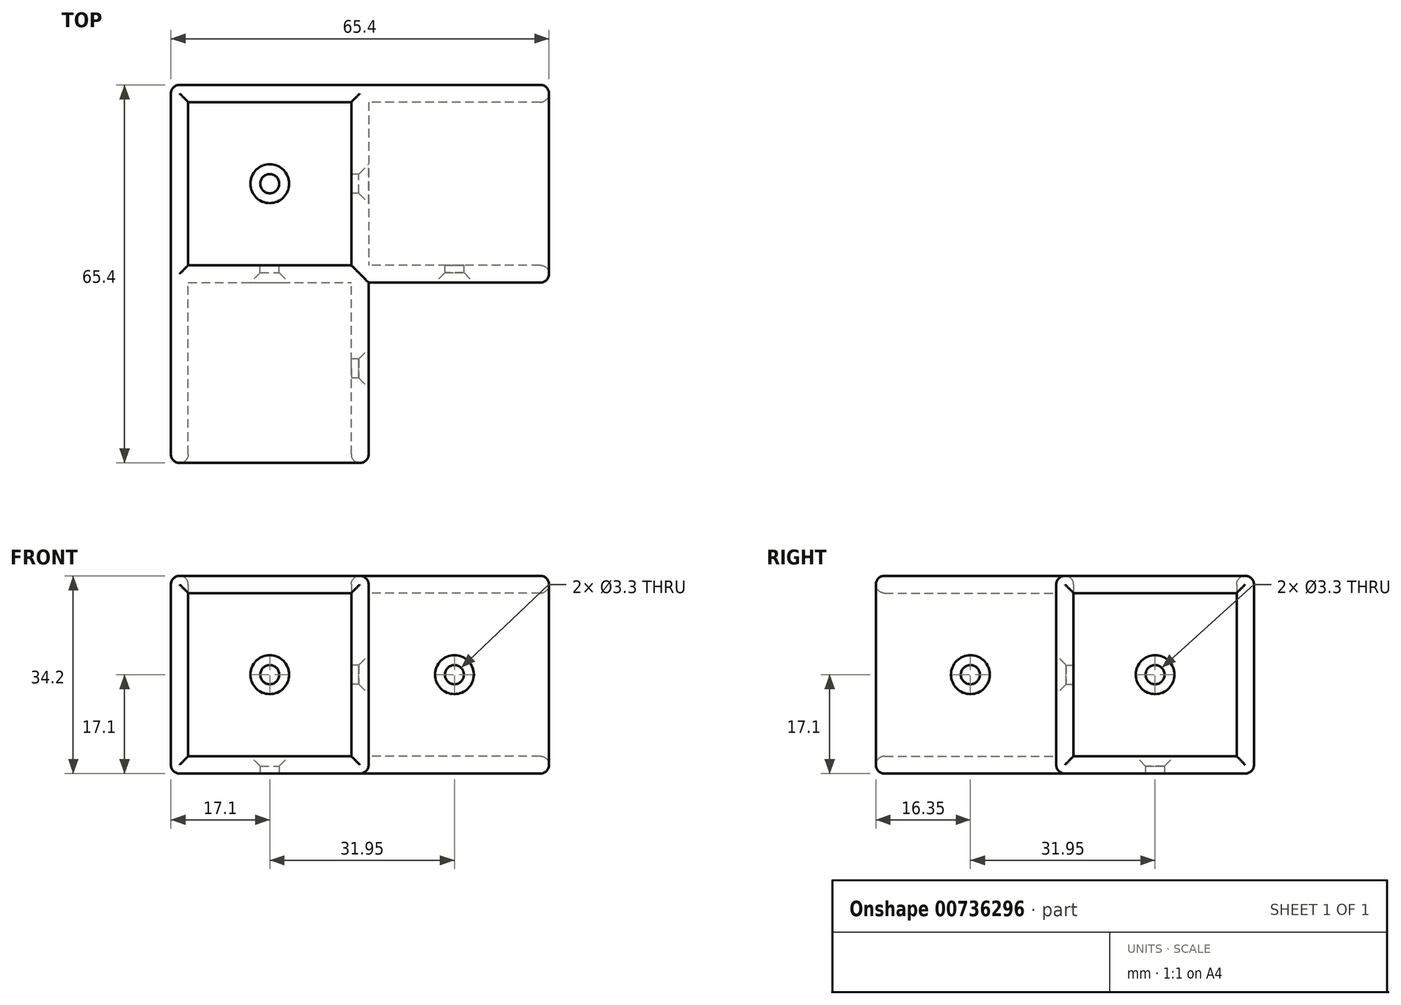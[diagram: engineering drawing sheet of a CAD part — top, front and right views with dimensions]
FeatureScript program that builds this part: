
annotation { "Feature Type Name" : "Feature", "Feature Type Description" : "" }
export const myFeature = defineFeature(function(context is Context, id is Id, definition is map)
    precondition{}
    {
        {
            var Q0;
            Q0=qCreatedBy(makeId("Top.planeOp"),FACE);
            var sketch = newSketch(context, id + "F0", { "sketchPlane" : qUnion([Q0])});
            skLineSegment(sketch, "E0.bottom", {"start": v(0, 0) * mm, "end": v(-28.2, 0) * mm});
            skLineSegment(sketch, "E0.top", {"start": v(0, 28.2) * mm, "end": v(-28.2, 28.2) * mm});
            skLineSegment(sketch, "E0.left", {"start": v(0, 0) * mm, "end": v(0, 28.2) * mm});
            skLineSegment(sketch, "E0.right", {"start": v(-28.2, 0) * mm, "end": v(-28.2, 28.2) * mm});
            skLineSegment(sketch, "E1.0", {"start": v(3, 31.2) * mm, "end": v(-31.2, 31.2) * mm});
            skLineSegment(sketch, "E1.1", {"start": v(3, -3) * mm, "end": v(3, 31.2) * mm});
            skLineSegment(sketch, "E1.2", {"start": v(3, -3) * mm, "end": v(-31.2, -3) * mm});
            skLineSegment(sketch, "E1.3", {"start": v(-31.2, -3) * mm, "end": v(-31.2, 31.2) * mm});
            skPoint(sketch, "E2", {"position": v(-14.1, 14.1) * mm});
            skSolve(sketch);
        }
        {
            var Q0;
            Q0=makeQuery(id+"F0.imprint","IMPRINT",FACE,{"disambiguationData":[TD([[makeQuery(id+"F0.imprint","IMPRINT",EDGE,{"derivedFrom":sQuery(id+"F0.wireOp",EDGE,"E0.bottom")}),1.0]])]});
            var Q1;
            Q1=makeQuery(id+"F0.imprint","IMPRINT",FACE,{"disambiguationData":[TD([[makeQuery(id+"F0.imprint","IMPRINT",EDGE,{"derivedFrom":sQuery(id+"F0.wireOp",EDGE,"E0.bottom")}),-1.0]])]});
            extrude(context, id + "F1", {"entities" : qUnion([Q0, Q1]), "oppositeDirection" : true, "depth" : 3 * mm, "offsetDistance" : 25 * mm});
        }
        {
            var Q0;
            Q0=makeQuery(id+"F0.imprint","IMPRINT",FACE,{"disambiguationData":[TD([[makeQuery(id+"F0.imprint","IMPRINT",EDGE,{"derivedFrom":sQuery(id+"F0.wireOp",EDGE,"E0.bottom")}),1.0]])]});
            extrude(context, id + "F2", {"entities" : qUnion([Q0]), "operationType" : NewBodyOperationType.ADD, "depth" : 31.2 * mm, "offsetDistance" : 25 * mm});
        }
        {
            var Q0;
            {var subQ0=sQuery(id+"F0.wireOp",EDGE,"E1.2");Q0=makeQuery(id+"F2.boolean.opBoolean","MERGE",FACE,{"derivedFrom":[makeQuery(id+"F1.opExtrude","SWEPT_FACE",FACE,{"disambiguationData":[OSD([subQ0])]}),makeQuery(id+"F2.opExtrude","SWEPT_FACE",FACE,{"disambiguationData":[OSD([subQ0])]})]});}
            var sketch = newSketch(context, id + "F3", { "sketchPlane" : qUnion([Q0])});
            skLineSegment(sketch, "E3.bottom", {"start": v(-31.2, 31.2) * mm, "end": v(3, 31.2) * mm});
            skLineSegment(sketch, "E3.top", {"start": v(-31.2, -3) * mm, "end": v(3, -3) * mm});
            skLineSegment(sketch, "E3.left", {"start": v(-31.2, 31.2) * mm, "end": v(-31.2, -3) * mm});
            skLineSegment(sketch, "E3.right", {"start": v(3, 31.2) * mm, "end": v(3, -3) * mm});
            skLineSegment(sketch, "E4.0", {"start": v(-28.2, 28.2) * mm, "end": v(0, 28.2) * mm});
            skLineSegment(sketch, "E4.1", {"start": v(-28.2, 28.2) * mm, "end": v(-28.2, 0) * mm});
            skLineSegment(sketch, "E4.2", {"start": v(-28.2, 0) * mm, "end": v(0, 0) * mm});
            skLineSegment(sketch, "E4.3", {"start": v(0, 28.2) * mm, "end": v(0, 0) * mm});
            skPoint(sketch, "E5", {"position": v(-14.1, 14.1) * mm});
            skSolve(sketch);
        }
        {
            var Q0;
            Q0=makeQuery(id+"F3.imprint","IMPRINT",FACE,{"disambiguationData":[TD([[makeQuery(id+"F3.imprint","IMPRINT",EDGE,{"derivedFrom":sQuery(id+"F3.wireOp",EDGE,"E3.bottom")}),1.0]])]});
            extrude(context, id + "F4", {"entities" : qUnion([Q0]), "operationType" : NewBodyOperationType.ADD, "depth" : 31.2 * mm, "offsetDistance" : 25 * mm});
        }
        {
            var Q0;
            {var subQ0=sQuery(id+"F0.wireOp",EDGE,"E1.1");Q0=makeQuery(id+"F4.boolean.opBoolean","MERGE",FACE,{"derivedFrom":[makeQuery(id+"F2.boolean.opBoolean","MERGE",FACE,{"derivedFrom":[makeQuery(id+"F1.opExtrude","SWEPT_FACE",FACE,{"disambiguationData":[OSD([subQ0])]}),makeQuery(id+"F2.opExtrude","SWEPT_FACE",FACE,{"disambiguationData":[OSD([subQ0])]})]}),makeQuery(id+"F4.opExtrude","SWEPT_FACE",FACE,{"disambiguationData":[OSD([sQuery(id+"F3.wireOp",EDGE,"E3.right")])]})]});}
            var sketch = newSketch(context, id + "F5", { "sketchPlane" : qUnion([Q0])});
            skLineSegment(sketch, "E6.bottom", {"start": v(31.2, 31.2) * mm, "end": v(-3, 31.2) * mm});
            skLineSegment(sketch, "E6.top", {"start": v(31.2, -3) * mm, "end": v(-3, -3) * mm});
            skLineSegment(sketch, "E6.left", {"start": v(31.2, 31.2) * mm, "end": v(31.2, -3) * mm});
            skLineSegment(sketch, "E6.right", {"start": v(-3, 31.2) * mm, "end": v(-3, -3) * mm});
            skLineSegment(sketch, "E7.0", {"start": v(28.2, 28.2) * mm, "end": v(0, 28.2) * mm});
            skLineSegment(sketch, "E7.1", {"start": v(28.2, 28.2) * mm, "end": v(28.2, 0) * mm});
            skLineSegment(sketch, "E7.2", {"start": v(28.2, 0) * mm, "end": v(0, 0) * mm});
            skLineSegment(sketch, "E7.3", {"start": v(0, 28.2) * mm, "end": v(0, 0) * mm});
            skPoint(sketch, "E8", {"position": v(14.1, 14.1) * mm});
            skSolve(sketch);
        }
        {
            var Q0;
            Q0 = qSketchRegion(id + "F5", true);
            extrude(context, id + "F6", {"entities" : qUnion([Q0]), "operationType" : NewBodyOperationType.ADD, "depth" : 31.2 * mm, "offsetDistance" : 25 * mm});
        }
        {
            var Q0;
            Q0=sQuery(id+"F0.wireOp",VERTEX,"E2");
            var Q1;
            Q1=sQuery(id+"F5.wireOp",VERTEX,"E8");
            var Q2;
            Q2=sQuery(id+"F3.wireOp",VERTEX,"E5");
            var Q3;
            Q3=makeQuery(id+"F1.opExtrude","SWEPT_BODY",BODY,{"disambiguationData":[OSD([sQuery(id+"F0.wireOp",EDGE,"E1.0"),sQuery(id+"F0.wireOp",EDGE,"E1.1"),sQuery(id+"F0.wireOp",EDGE,"E1.2"),sQuery(id+"F0.wireOp",EDGE,"E1.3")])]});
            hole(context, id + "F7", {"style" : HoleStyle.C_SINK, "endStyle" : HoleEndStyle.BLIND, "standardTappedOrClearance" : lookupTablePath({ "standard" : "ISO", "fit" : "Normal", "size" : "M3", "type" : "Clearance" }), "standardBlindInLast" : lookupTablePath({ "fit" : "Standard", "standard" : "ISO", "size" : "M3", "type" : "Clearance" }), "holeDiameter" : 3.3 * mm, "cSinkDiameter" : 6.72 * mm, "cSinkAngle" : 90 * degree, "majorDiameter" : 5 * mm, "holeDepth" : 13.5 * mm, "isTappedThrough" : true, "tappedDepth" : 12 * mm, "tapClearance" : 3, "startFromSketch" : true, "locations" : qUnion([Q0, Q1, Q2]), "scope" : qUnion([Q3])});
        }
        {
            var Q0;
            Q0=makeQuery(id+"F4.boolean.opBoolean","MERGE",EDGE,{"derivedFrom":[makeQuery(id+"F2.opExtrude","CAP_EDGE",EDGE,{"disambiguationData":[OSD([sQuery(id+"F0.wireOp",EDGE,"E1.3")])],"isStart":false}),makeQuery(id+"F4.opExtrude","SWEPT_EDGE",EDGE,{"disambiguationData":[OSD([sQuery(id+"F3.wireOp",EDGE,"E3.bottom"),sQuery(id+"F3.wireOp",EDGE,"E3.left")])]})]});
            var Q1;
            Q1=makeQuery(id+"F6.boolean.opBoolean","MERGE",EDGE,{"derivedFrom":[makeQuery(id+"F2.opExtrude","CAP_EDGE",EDGE,{"disambiguationData":[OSD([sQuery(id+"F0.wireOp",EDGE,"E1.0")])],"isStart":false}),makeQuery(id+"F6.opExtrude","SWEPT_EDGE",EDGE,{"disambiguationData":[OSD([sQuery(id+"F5.wireOp",EDGE,"E6.bottom"),sQuery(id+"F5.wireOp",EDGE,"E6.left")])]})]});
            var Q2;
            Q2=makeQuery(id+"F6.opExtrude","CAP_EDGE",EDGE,{"disambiguationData":[OSD([sQuery(id+"F5.wireOp",EDGE,"E6.bottom")])],"isStart":false});
            var Q3;
            Q3=makeQuery(id+"F6.opExtrude","SWEPT_EDGE",EDGE,{"disambiguationData":[OSD([sQuery(id+"F0.wireOp",EDGE,"E1.1"),sQuery(id+"F3.wireOp",EDGE,"E3.bottom"),sQuery(id+"F3.wireOp",EDGE,"E3.right"),sQuery(id+"F5.wireOp",EDGE,"E6.bottom"),sQuery(id+"F5.wireOp",EDGE,"E6.right")])]});
            var Q4;
            Q4=makeQuery(id+"F4.boolean.opBoolean","MERGE",EDGE,{"derivedFrom":[makeQuery(id+"F2.opExtrude","CAP_EDGE",EDGE,{"disambiguationData":[OSD([sQuery(id+"F0.wireOp",EDGE,"E1.1")])],"isStart":false}),makeQuery(id+"F4.opExtrude","SWEPT_EDGE",EDGE,{"disambiguationData":[OSD([sQuery(id+"F3.wireOp",EDGE,"E3.bottom"),sQuery(id+"F3.wireOp",EDGE,"E3.right")])]})]});
            var Q5;
            Q5=makeQuery(id+"F4.opExtrude","CAP_EDGE",EDGE,{"disambiguationData":[OSD([sQuery(id+"F3.wireOp",EDGE,"E3.bottom")])],"isStart":false});
            var Q6;
            Q6=makeQuery(id+"F2.opExtrude","CAP_EDGE",EDGE,{"disambiguationData":[OSD([sQuery(id+"F0.wireOp",EDGE,"E0.bottom")])],"isStart":false});
            var Q7;
            Q7=makeQuery(id+"F2.opExtrude","CAP_EDGE",EDGE,{"disambiguationData":[OSD([sQuery(id+"F0.wireOp",EDGE,"E0.left")])],"isStart":false});
            var Q8;
            Q8=makeQuery(id+"F2.opExtrude","CAP_EDGE",EDGE,{"disambiguationData":[OSD([sQuery(id+"F0.wireOp",EDGE,"E0.right")])],"isStart":false});
            var Q9;
            Q9=makeQuery(id+"F2.opExtrude","CAP_EDGE",EDGE,{"disambiguationData":[OSD([sQuery(id+"F0.wireOp",EDGE,"E0.top")])],"isStart":false});
            var Q10;
            Q10=makeQuery(id+"F6.opExtrude","SWEPT_EDGE",EDGE,{"disambiguationData":[OSD([sQuery(id+"F0.wireOp",EDGE,"E1.1"),sQuery(id+"F3.wireOp",EDGE,"E3.top"),sQuery(id+"F3.wireOp",EDGE,"E3.right"),sQuery(id+"F5.wireOp",EDGE,"E6.top"),sQuery(id+"F5.wireOp",EDGE,"E6.right")])]});
            var Q11;
            Q11=makeQuery(id+"F4.boolean.opBoolean","MERGE",EDGE,{"derivedFrom":[makeQuery(id+"F1.opExtrude","CAP_EDGE",EDGE,{"disambiguationData":[OSD([sQuery(id+"F0.wireOp",EDGE,"E1.1")])],"isStart":false}),makeQuery(id+"F4.opExtrude","SWEPT_EDGE",EDGE,{"disambiguationData":[OSD([sQuery(id+"F3.wireOp",EDGE,"E3.top"),sQuery(id+"F3.wireOp",EDGE,"E3.right")])]})]});
            var Q12;
            Q12=makeQuery(id+"F4.opExtrude","CAP_EDGE",EDGE,{"disambiguationData":[OSD([sQuery(id+"F3.wireOp",EDGE,"E3.top")])],"isStart":false});
            var Q13;
            Q13=makeQuery(id+"F4.boolean.opBoolean","MERGE",EDGE,{"derivedFrom":[makeQuery(id+"F1.opExtrude","CAP_EDGE",EDGE,{"disambiguationData":[OSD([sQuery(id+"F0.wireOp",EDGE,"E1.3")])],"isStart":false}),makeQuery(id+"F4.opExtrude","SWEPT_EDGE",EDGE,{"disambiguationData":[OSD([sQuery(id+"F3.wireOp",EDGE,"E3.top"),sQuery(id+"F3.wireOp",EDGE,"E3.left")])]})]});
            var Q14;
            Q14=makeQuery(id+"F6.boolean.opBoolean","MERGE",EDGE,{"derivedFrom":[makeQuery(id+"F1.opExtrude","CAP_EDGE",EDGE,{"disambiguationData":[OSD([sQuery(id+"F0.wireOp",EDGE,"E1.0")])],"isStart":false}),makeQuery(id+"F6.opExtrude","SWEPT_EDGE",EDGE,{"disambiguationData":[OSD([sQuery(id+"F5.wireOp",EDGE,"E6.top"),sQuery(id+"F5.wireOp",EDGE,"E6.left")])]})]});
            var Q15;
            Q15=makeQuery(id+"F6.opExtrude","CAP_EDGE",EDGE,{"disambiguationData":[OSD([sQuery(id+"F5.wireOp",EDGE,"E6.top")])],"isStart":false});
            var Q16;
            Q16=makeQuery(id+"F4.opExtrude","CAP_EDGE",EDGE,{"disambiguationData":[OSD([sQuery(id+"F3.wireOp",EDGE,"E3.right")])],"isStart":false});
            var Q17;
            Q17=makeQuery(id+"F4.opExtrude","CAP_EDGE",EDGE,{"disambiguationData":[OSD([sQuery(id+"F3.wireOp",EDGE,"E4.3")])],"isStart":false});
            var Q18;
            Q18=makeQuery(id+"F4.opExtrude","CAP_EDGE",EDGE,{"disambiguationData":[OSD([sQuery(id+"F3.wireOp",EDGE,"E4.1")])],"isStart":false});
            var Q19;
            Q19=makeQuery(id+"F4.opExtrude","CAP_EDGE",EDGE,{"disambiguationData":[OSD([sQuery(id+"F3.wireOp",EDGE,"E3.left")])],"isStart":false});
            var Q20;
            Q20=makeQuery(id+"F4.opExtrude","CAP_EDGE",EDGE,{"disambiguationData":[OSD([sQuery(id+"F3.wireOp",EDGE,"E4.0")])],"isStart":false});
            var Q21;
            Q21=makeQuery(id+"F4.opExtrude","CAP_EDGE",EDGE,{"disambiguationData":[OSD([sQuery(id+"F3.wireOp",EDGE,"E4.2")])],"isStart":false});
            var Q22;
            {var subQ0=sQuery(id+"F0.wireOp",EDGE,"E1.3");var subQ1=sQuery(id+"F0.wireOp",EDGE,"E1.0");Q22=makeQuery(id+"F2.boolean.opBoolean","MERGE",EDGE,{"derivedFrom":[makeQuery(id+"F1.opExtrude","SWEPT_EDGE",EDGE,{"disambiguationData":[OSD([subQ1,subQ0])]}),makeQuery(id+"F2.opExtrude","SWEPT_EDGE",EDGE,{"disambiguationData":[OSD([subQ1,subQ0])]})]});}
            var Q23;
            Q23=makeQuery(id+"F6.opExtrude","CAP_EDGE",EDGE,{"disambiguationData":[OSD([sQuery(id+"F5.wireOp",EDGE,"E6.left")])],"isStart":false});
            var Q24;
            Q24=makeQuery(id+"F6.opExtrude","CAP_EDGE",EDGE,{"disambiguationData":[OSD([sQuery(id+"F5.wireOp",EDGE,"E7.1")])],"isStart":false});
            var Q25;
            Q25=makeQuery(id+"F6.opExtrude","CAP_EDGE",EDGE,{"disambiguationData":[OSD([sQuery(id+"F5.wireOp",EDGE,"E7.3")])],"isStart":false});
            var Q26;
            Q26=makeQuery(id+"F6.opExtrude","CAP_EDGE",EDGE,{"disambiguationData":[OSD([sQuery(id+"F5.wireOp",EDGE,"E6.right")])],"isStart":false});
            var Q27;
            Q27=makeQuery(id+"F6.opExtrude","CAP_EDGE",EDGE,{"disambiguationData":[OSD([sQuery(id+"F5.wireOp",EDGE,"E7.2")])],"isStart":false});
            var Q28;
            Q28=makeQuery(id+"F6.opExtrude","CAP_EDGE",EDGE,{"disambiguationData":[OSD([sQuery(id+"F5.wireOp",EDGE,"E7.0")])],"isStart":false});
            fillet(context, id + "F8", {"entities" : qUnion([Q0, Q1, Q2, Q3, Q4, Q5, Q6, Q7, Q8, Q9, Q10, Q11, Q12, Q13, Q14, Q15, Q16, Q17, Q18, Q19, Q20, Q21, Q22, Q23, Q24, Q25, Q26, Q27, Q28]), "radius" : 1.5 * mm, "tangentPropagation" : true, "allowEdgeOverflow" : false});
        }
        {
            var Q0;
            {var subQ0=sQuery(id+"F3.wireOp",EDGE,"E3.bottom");var subQ3=sQuery(id+"F0.wireOp",EDGE,"E1.1");var subQ5=sQuery(id+"F3.wireOp",EDGE,"E3.right");Q0=makeQuery(id+"F6.boolean.opBoolean","SPLIT",FACE,{"disambiguationData":[TD([makeQuery(id+"F4.opExtrude","SWEPT_FACE",FACE,{"disambiguationData":[OSD([subQ0])]})])],"derivedFrom":makeQuery(id+"F4.boolean.opBoolean","MERGE",FACE,{"derivedFrom":[makeQuery(id+"F2.boolean.opBoolean","MERGE",FACE,{"derivedFrom":[makeQuery(id+"F1.opExtrude","SWEPT_FACE",FACE,{"disambiguationData":[OSD([subQ3])]}),makeQuery(id+"F2.opExtrude","SWEPT_FACE",FACE,{"disambiguationData":[OSD([subQ3])]})]}),makeQuery(id+"F4.opExtrude","SWEPT_FACE",FACE,{"disambiguationData":[OSD([subQ5])]})]})});}
            var sketch = newSketch(context, id + "F9", { "sketchPlane" : qUnion([Q0])});
            skPoint(sketch, "E9", {"position": v(-17.85, 14.1) * mm});
            skSolve(sketch);
        }
        {
            var Q0;
            Q0=makeQuery(id+"F6.opExtrude","SWEPT_FACE",FACE,{"disambiguationData":[OSD([sQuery(id+"F5.wireOp",EDGE,"E6.right")])]});
            var sketch = newSketch(context, id + "F10", { "sketchPlane" : qUnion([Q0])});
            skPoint(sketch, "E10", {"position": v(17.85, 14.1) * mm});
            skSolve(sketch);
        }
        {
            var Q0;
            Q0=sQuery(id+"F10.wireOp",VERTEX,"E10");
            var Q1;
            Q1=sQuery(id+"F9.wireOp",VERTEX,"E9");
            var Q2;
            Q2=makeQuery(id+"F1.opExtrude","SWEPT_BODY",BODY,{"disambiguationData":[OSD([sQuery(id+"F0.wireOp",EDGE,"E1.0"),sQuery(id+"F0.wireOp",EDGE,"E1.1"),sQuery(id+"F0.wireOp",EDGE,"E1.2"),sQuery(id+"F0.wireOp",EDGE,"E1.3")])]});
            hole(context, id + "F11", {"style" : HoleStyle.C_SINK, "endStyle" : HoleEndStyle.BLIND, "standardTappedOrClearance" : lookupTablePath({ "standard" : "ISO", "fit" : "Normal", "size" : "M3", "type" : "Clearance" }), "standardBlindInLast" : lookupTablePath({ "fit" : "Standard", "standard" : "ISO", "size" : "M3", "type" : "Clearance" }), "holeDiameter" : 3.3 * mm, "cSinkDiameter" : 6.72 * mm, "cSinkAngle" : 90 * degree, "majorDiameter" : 5 * mm, "holeDepth" : 13.5 * mm, "isTappedThrough" : true, "tappedDepth" : 12 * mm, "tapClearance" : 3, "startFromSketch" : true, "locations" : qUnion([Q0, Q1]), "scope" : qUnion([Q2])});
        }
    });
